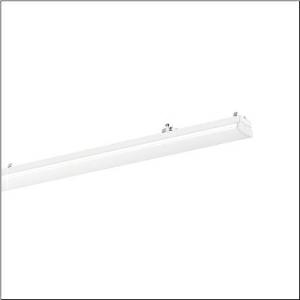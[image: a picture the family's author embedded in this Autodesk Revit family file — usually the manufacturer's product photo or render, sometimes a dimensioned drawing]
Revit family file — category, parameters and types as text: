
# Revit family: licross_11_recessed_opal_ho_51tl1dmv4g5m
name_source: partatom
category: Lighting Fixtures
units: mm (PartAtom-declared; Revit-internal decimal feet)

## family parameters
Cut with Voids When Loaded = No
Host = Face
Light Source = No
Part Type = Normal
Room Calculation Point = No
Round Connector Dimension = Use Diameter
Shared = No

## types (1)
- --- (1 x LED, 16760 lm, 89.2 W, 4000K)
    Apparent Load = 89 VA
    CIE Flux Codes = 44 73 91 87 100
    Color Rendering = 80
    Color Temperature = 4000K
    Default Elevation = 1800 mm
    Description = Licross 11 recessed opal HO, luminaire insert, of sheet steel, coil coated, white, length: 2.250mm, width: 76mm, height: 87mm, LED rated luminous flux: 16.760lm, light colour: 840, SDCM (Standard Deviation of Colour Matching)MacAdam ≤ 2 SDCM (initial), control gear: ON/OFF Multilumen, with plug, 3-pole, with phase selection, mains connection: 220..240V, AC, 50/60Hz, rated input power: 89W, internal wiring halogen-free, primary optical cover: cover, of PMMA, light emission: direct with ceiling illumination distribution, primary light characteristic: symmetric, protection rating (complete): IP40, insulation class (complete): insulation class I (protective earthing), certification: CE, ENEC, VDE, UKCA, protection symbol: D if used in an environment without relevant dust loads with corresponding accessories, impact resistance: IK06, permissible ambient temperature for indoor applications: -35..+35°C, corresponds to IFS (International Featured Standards) requirements for safety and quality in the food industry, reducing of maximum allowable ambient temperature of 5°C with ceiling mounting, The light source and the operating device comply with the requirements of the Ecodesign Regulation (EU) 2019/2020 and are replaceable in accordance with this regulation, packaging unit: 1 piece
    Height = 83 mm
    Lamp = 1 x LED
    Lamp Light Flux = 16760 lm
    Lamp Power = 89.2 W
    Lamp count = 1
    Length = 2250 mm
    Luminous efficacy = 188 lm/W
    Manufacturer = Siteco
    ModVariant = No
    Model = 51TL1DMV4G5M
    Mounting Place = Ceiling
    Mounting Type = Pendant
    Number of Poles = 1
    OnlyDefault = Yes
    Power Factor = 1
    Product Name = Licross 11 recessed opal HO
    Product group = luminaire insert | ceiling pendant
    ProductGroupID = 901
    Protection Class = Protection class I
    Protection Degree = IP 40
    RLX_Detail_Level = 1
    RLX_Emergency_Light_Flux = 0 lm
    RLX_Emergency_Type = 0
    RLX_Emergency_Type_DB = No
    RlxData = <blob elided: 24733 chars, md5=7eb43cc4>
    Socket = socket
    Standby Power = 0 W
    System Light Flux = 16760 lm
    System Power = 89 W
    Type Comments = factory setting: luminous flux: 100 % | (A | C | E) | 210 mA
    Type Image = l_1313666.jpg
    URL = http://relux.com
    VarID = @adj_083589
    Voltage = 0 V
    Weight = 0.00 kg
    Width = 76 mm

## geometry (parser evidence)
native form markers: Blend x4, Sweep x13
no freeform markers — native parametric forms only
